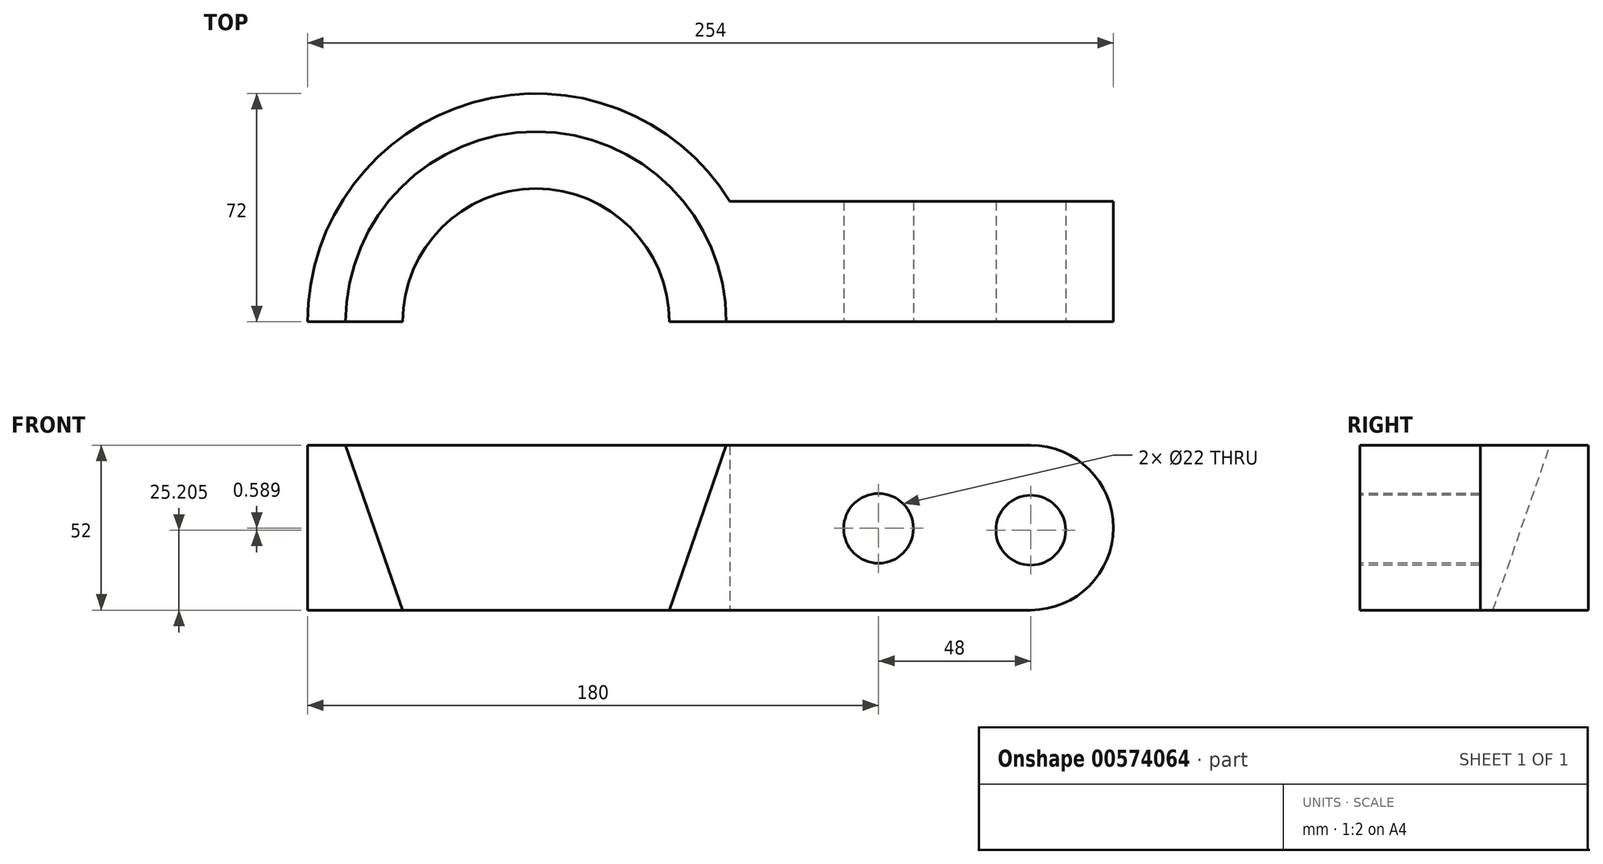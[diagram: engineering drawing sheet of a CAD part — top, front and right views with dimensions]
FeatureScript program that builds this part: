
annotation { "Feature Type Name" : "Feature", "Feature Type Description" : "" }
export const myFeature = defineFeature(function(context is Context, id is Id, definition is map)
    precondition{}
    {
        {
            var Q0;
            Q0=qCreatedBy(makeId("Top.planeOp"),FACE);
            var sketch = newSketch(context, id + "F0", { "sketchPlane" : qUnion([Q0])});
            skLineSegment(sketch, "E0.top", {"start": v(61.16, 38) * mm, "end": v(182, 38) * mm});
            skLineSegment(sketch, "E0.right", {"start": v(182, 0) * mm, "end": v(182, 38) * mm});
            skArc(sketch, "E1", {"start": v(-72, 0) * mm, "mid": v(-19.76, 69.24) * mm, "end": v(61.16, 38) * mm});
            skLineSegment(sketch, "E2", {"start": v(-72, 0) * mm, "end": v(182, 0) * mm});
            skSolve(sketch);
        }
        {
            var Q0;
            Q0 = qSketchRegion(id + "F0", true);
            extrude(context, id + "F1", {"entities" : qUnion([Q0]), "depth" : 52 * mm, "offsetDistance" : 25 * mm});
        }
        {
            var Q0;
            Q0=makeQuery(id+"F1.opExtrude","SWEPT_FACE",FACE,{"disambiguationData":[OSD([sQuery(id+"F0.wireOp",EDGE,"E2")])]});
            var sketch = newSketch(context, id + "F2", { "sketchPlane" : qUnion([Q0])});
            skLineSegment(sketch, "E3", {"start": v(0, 52) * mm, "end": v(0, 0) * mm});
            skLineSegment(sketch, "E4", {"start": v(0, 0) * mm, "end": v(42, 0) * mm});
            skLineSegment(sketch, "E5", {"start": v(42, 0) * mm, "end": v(60, 52) * mm});
            skLineSegment(sketch, "E6", {"start": v(60, 52) * mm, "end": v(0, 52) * mm});
            skSolve(sketch);
        }
        {
            var Q0;
            Q0 = qSketchRegion(id + "F2", true);
            var Q1;
            Q1=sQuery(id+"F2.wireOp",EDGE,"E3");
            revolve(context, id + "F3", {"operationType" : NewBodyOperationType.REMOVE, "entities" : qUnion([Q0]), "axis" : qUnion([Q1]), "revolveType" : RevolveType.FULL, "oppositeDirection" : true});
        }
        {
            var Q0;
            {var subQ0=sQuery(id+"F0.wireOp",EDGE,"E2");var subQ2=sQuery(id+"F0.wireOp",EDGE,"E0.right");Q0=makeQuery(id+"F3.boolean.opBoolean","SPLIT",FACE,{"disambiguationData":[TD([makeQuery(id+"F1.opExtrude","SWEPT_FACE",FACE,{"disambiguationData":[OSD([subQ2])]})])],"derivedFrom":makeQuery(id+"F1.opExtrude","SWEPT_FACE",FACE,{"disambiguationData":[OSD([subQ0])]})});}
            var sketch = newSketch(context, id + "F4", { "sketchPlane" : qUnion([Q0])});
            skCircle(sketch, "E7", {"center": v(108, 25.8) * mm, "radius": 11 * mm});
            skCircle(sketch, "E8", {"center": v(156, 25.2) * mm, "radius": 11 * mm});
            skSolve(sketch);
        }
        {
            var Q0;
            Q0=makeQuery(id+"F4.imprint","IMPRINT",FACE,{"disambiguationData":[TD([[makeQuery(id+"F4.imprint","IMPRINT",EDGE,{"derivedFrom":sQuery(id+"F4.wireOp",EDGE,"E7")}),1.0]])]});
            var Q1;
            Q1=makeQuery(id+"F4.imprint","IMPRINT",FACE,{"disambiguationData":[TD([[makeQuery(id+"F4.imprint","IMPRINT",EDGE,{"derivedFrom":sQuery(id+"F4.wireOp",EDGE,"E8")}),1.0]])]});
            extrude(context, id + "F5", {"entities" : qUnion([Q0, Q1]), "operationType" : NewBodyOperationType.REMOVE, "oppositeDirection" : true, "depth" : 38 * mm, "offsetDistance" : 25 * mm});
        }
        {
            var Q0;
            Q0=makeQuery(id+"F1.opExtrude","CAP_EDGE",EDGE,{"disambiguationData":[OSD([sQuery(id+"F0.wireOp",EDGE,"E0.right")])],"isStart":false});
            var Q1;
            Q1=makeQuery(id+"F1.opExtrude","CAP_EDGE",EDGE,{"disambiguationData":[OSD([sQuery(id+"F0.wireOp",EDGE,"E0.right")])],"isStart":true});
            fillet(context, id + "F6", {"entities" : qUnion([Q0, Q1]), "radius" : 26 * mm, "tangentPropagation" : true, "allowEdgeOverflow" : false});
        }
    });
